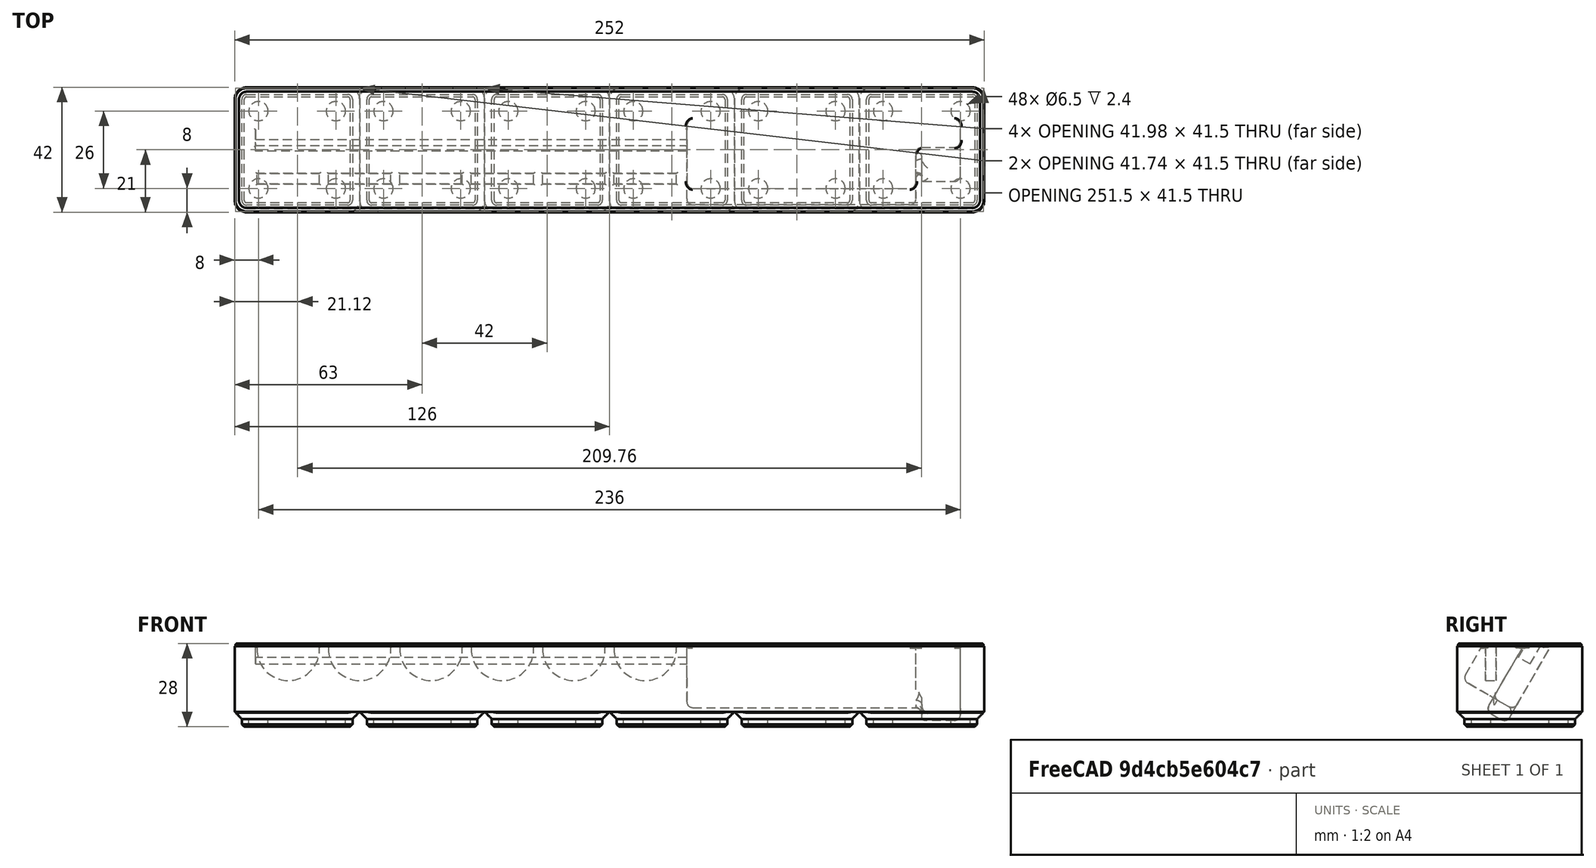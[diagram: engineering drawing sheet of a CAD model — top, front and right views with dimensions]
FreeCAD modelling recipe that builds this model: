
FCSTD DOCUMENT  (FreeCAD 0.21R)
Label: MyGridfinity 6x1x4
License: Creative Commons Attribution
LicenseURL: http://creativecommons.org/licenses/by/4.0/
objects: Sketcher::SketchObject×15, PartDesign::Pocket×5, PartDesign::LinearPattern×3, PartDesign::Plane×2, PartDesign::Pad×2, PartDesign::Body×2, PartDesign::FeatureBase×2, PartDesign::Fillet×2, App::FeaturePython×1, PartDesign::AdditivePipe×1, PartDesign::SubtractiveLoft×1, PartDesign::Hole×1, PartDesign::MultiTransform×1, Mesh::Feature×1, PartDesign::SubShapeBinder×1
note: 50 computed .brp shape members not serialized (recipe doc carries the construction recipe); baked Part::Feature solids carry a one-line shape summary decoded from their .brp

FEATURE [App::FeaturePython] dd  # WARN: FeaturePython — macro-defined, semantics opaque (R4)
  DynamicData = Created with DynamicData (v2.46) workbench. | This is a simple container object built | for holding custom properties.
  ddBase_screw_diameter = 3
  ddBase_screw_hole_depth = 2.6
  ddBottom_chamfer = 0.8
  ddCell_center = 21
  ddClearance = 0.25
  ddColumns = 6
  ddCorner_fillet = 4
  ddFrame_height = 5
  ddFrame_width = 2.4
  ddGrid_size = 42
  ddHeight = 4
  ddMagnet_diameter = 6.5
  ddMagnet_inset = 8
  ddMagnet_thickness = 2.4
  ddRows = 1
  ddSet_screw_holes = true
  ddStorage_height = 28
  ddStorage_height_unit = 7
  ddTotal_length = 42
  ddTotal_width = 252
  ddWall_thickness = 1.2
  expr: ddBase_screw_hole_depth = max(ddSet_screw_holes * (ddFrame_height - ddMagnet_thickness); 1e-06mm)
  expr: ddCell_center = ddGrid_size / 2
  expr: ddStorage_height = max(ddStorage_height_unit * ddHeight; ddFrame_height + ddWall_thickness)
  expr: ddStorage_height_unit = ddGrid_size / 6
  expr: ddTotal_length = ddRows * ddGrid_size
  expr: ddTotal_width = ddColumns * ddGrid_size
FEATURE [Sketcher::SketchObject] Sketch005  label="Sketch_storage_wall_profile"
  AttachmentOffset = pos=(0,0,21) rot=(0,0,1;0rad)
  FullyConstrained = true
  MapMode = 5
  Placement = pos=(21,-4.7e-15,4.7e-15) rot=(0.57735,0.57735,0.57735;2.0944rad)
  Support = -> [YZ_Plane001]
  expr: .AttachmentOffset.Base.z = dd.ddCell_center
  expr: Constraints[16] = dd.ddFrame_height - dd.ddClearance
  expr: Constraints[17] = dd.ddBottom_chamfer
  expr: Constraints[26] = dd.ddWall_thickness
  expr: Constraints[27] = dd.ddWall_thickness
  expr: Constraints[28] = dd.ddStorage_height
  expr: Constraints[47] = dd.ddWall_thickness
  expr: Constraints[6] = dd.ddClearance
  expr: Constraints[7] = dd.ddFrame_width - dd.ddClearance
  sketch-geometry (17):
    g0: LineSegment StartX=0.25 StartY=0 StartZ=0 EndX=0.25 EndY=27.4 EndZ=0
    g1: LineSegment StartX=0.25 StartY=27.4 StartZ=0 EndX=0.85 EndY=27.4 EndZ=0
    g2: LineSegment StartX=0.85 StartY=27.4 StartZ=0 EndX=0.425736 EndY=26.9757 EndZ=0
    g3: LineSegment StartX=0.425736 StartY=26.9757 StartZ=0 EndX=2.15 EndY=25.2515 EndZ=0
    g4: LineSegment StartX=2.15 StartY=25.2515 StartZ=0 EndX=0 EndY=27.4015 EndZ=0
    g5: LineSegment StartX=2.15 StartY=25.2515 StartZ=0 EndX=2.15 EndY=23.4515 EndZ=0
    g6: LineSegment StartX=2.15 StartY=23.4515 StartZ=0 EndX=2.95 EndY=22.6515 EndZ=0
    g7: LineSegment StartX=2.95 StartY=22.6515 StartZ=0 EndX=2.95 EndY=21.4515 EndZ=0
    g8: LineSegment StartX=2.95 StartY=21.4515 StartZ=0 EndX=1.45 EndY=19.9515 EndZ=0
    g9: LineSegment StartX=1.45 StartY=19.9515 StartZ=0 EndX=1.45 EndY=-8.04853 EndZ=0
    g10: LineSegment StartX=1.45 StartY=-8.04853 StartZ=0 EndX=0.25 EndY=-8.04853 EndZ=0
    g11: LineSegment StartX=0.85 StartY=27.4 StartZ=0 EndX=0.85 EndY=28 EndZ=0
    g12: LineSegment StartX=1.45 StartY=19.9515 StartZ=0 EndX=1.45 EndY=28 EndZ=0
    g13: LineSegment StartX=0.85 StartY=28 StartZ=0 EndX=1.45 EndY=28 EndZ=0
    g14: LineSegment StartX=0.25 StartY=-8.04853 StartZ=0 EndX=0.25 EndY=0 EndZ=0
    g15: ArcOfCircle CenterX=0.85 CenterY=27.4 CenterZ=0 NormalX=0 NormalY=0 NormalZ=1 AngleXU=0 Radius=0.6 StartAngle=1.5708 EndAngle=3.14159
    g16: ArcOfCircle CenterX=0.85 CenterY=27.4 CenterZ=0 NormalX=0 NormalY=0 NormalZ=1 AngleXU=0 Radius=0.6 StartAngle=3.92699 EndAngle=7.85398
  constraints (48):
    c: Vertical(g0)
    c: Coincident(g1,g0)
    c: Horizontal(g1)
    c: Coincident(g2,g1)
    c: Coincident(g3,g2)
    c: Perpendicular(g3,g2)
    c: DistanceX(g-1,g0) = 0.25
    c: DistanceX(g-1,g3) = 2.15
    c: Coincident(g4,g3)
    c: PointOnObject(g4,g-2)
    c: PointOnObject(g2,g4)
    c: Angle(g-2,g4) = 0.785398
    c: Coincident(g5,g3)
    c: Vertical(g5)
    c: Coincident(g6,g5)
    c: Parallel(g4,g6)
    c: DistanceY(g6,g4) = 4.75
    c: DistanceX(g5,g6) = 0.8
    c: Coincident(g7,g6)
    c: Vertical(g7)
    c: Coincident(g8,g7)
    c: Coincident(g9,g8)
    c: Vertical(g9)
    c: Coincident(g10,g9)
    c: Horizontal(g10)
    c: Perpendicular(g8,g4)
    c: DistanceY(g7,g6) = 1.2
    c: DistanceX(g0,g9) = 1.2
    c: DistanceY(g-1,g11) = 28
    c: Coincident(g12,g8)
    c: Vertical(g12)
    c: Coincident(g13,g11)
    c: Coincident(g13,g12)
    c: Horizontal(g13)
    c: PointOnObject(g0,g-1)
    c: Coincident(g14,g10)
    c: Coincident(g14,g0)
    c: Vertical(g14)
    c: Equal(g12,g14)
    c: Vertical(g11)
    c: Coincident(g15,g1)
    c: Coincident(g15,g0)
    c: Coincident(g15,g11)
    c: Coincident(g16,g15)
    c: Coincident(g16,g15)
    c: Coincident(g16,g3)
    c: Coincident(g11,g15)
    c: Diameter(g15) = 1.2
FEATURE [Sketcher::SketchObject] Sketch006  label="Sketch_storage_wall_path"
  FullyConstrained = true
  MapMode = 5
  Support = -> [XY_Plane001]
  expr: Constraints[21] = dd.ddCorner_fillet
  expr: Constraints[22] = dd.ddTotal_width
  expr: Constraints[23] = dd.ddTotal_length
  sketch-geometry (10):
    g0: ArcOfCircle CenterX=4 CenterY=4 CenterZ=0 NormalX=0 NormalY=0 NormalZ=1 AngleXU=0 Radius=4 StartAngle=3.14159 EndAngle=4.71239
    g1: LineSegment StartX=0 StartY=4 StartZ=0 EndX=0 EndY=38 EndZ=0
    g2: ArcOfCircle CenterX=4 CenterY=38 CenterZ=0 NormalX=0 NormalY=0 NormalZ=1 AngleXU=0 Radius=4 StartAngle=1.5708 EndAngle=3.14159
    g3: LineSegment StartX=4 StartY=42 StartZ=0 EndX=248 EndY=42 EndZ=0
    g4: ArcOfCircle CenterX=248 CenterY=38 CenterZ=0 NormalX=0 NormalY=0 NormalZ=1 AngleXU=0 Radius=4 StartAngle=0 EndAngle=1.5708
    g5: LineSegment StartX=252 StartY=38 StartZ=0 EndX=252 EndY=4 EndZ=0
    g6: ArcOfCircle CenterX=248 CenterY=4 CenterZ=0 NormalX=0 NormalY=0 NormalZ=1 AngleXU=0 Radius=4 StartAngle=4.71239 EndAngle=6.28319
    g7: LineSegment StartX=248 StartY=0 StartZ=0 EndX=4 EndY=0 EndZ=0
    g8: GeomPoint X=0 Y=0 Z=0
    g9: GeomPoint X=252 Y=42 Z=0
  constraints (24):
    c: Tangent(g0,g1) = 1.5708
    c: Tangent(g1,g2) = 1.5708
    c: Tangent(g2,g3) = 1.5708
    c: Tangent(g3,g4) = 1.5708
    c: Tangent(g4,g5) = 1.5708
    c: Tangent(g5,g6) = 1.5708
    c: Tangent(g6,g7) = 1.5708
    c: Tangent(g7,g0) = 1.5708
    c: Horizontal(g3)
    c: Horizontal(g7)
    c: Vertical(g1)
    c: Vertical(g5)
    c: Equal(g0,g2)
    c: Equal(g2,g4)
    c: Equal(g4,g6)
    c: PointOnObject(g8,g1)
    c: PointOnObject(g8,g7)
    c: PointOnObject(g9,g3)
    c: PointOnObject(g9,g5)
    c: PointOnObject(g8,g-2)
    c: PointOnObject(g0,g-1)
    c: Radius(g0) = 4
    c: DistanceX(g0,g5) = 252
    c: DistanceY(g0,g2) = 42
FEATURE [PartDesign::AdditivePipe] AdditivePipe  label="AdditivePipe_storage_wall"
  AuxilleryCurvelinear = true
  AuxillerySpineTangent = false
  Binormal = (0,0,0)
  Mode = 0
  Placement = pos=(0,0,0) rot=(0.57735,0.57735,0.57735;2.0944rad)
  Profile = -> Sketch005
  Refine = true
  Spine = -> Sketch006
  SpineTangent = false
  Transformation = 0
  Transition = 0
FEATURE [PartDesign::Plane] DatumPlane  label="DatumPlane_frame_height"
  AttachmentOffset = pos=(0,0,5) rot=(0,0,1;0rad)
  Length = 304.246
  MapMode = 5
  Placement = pos=(0,0,5) rot=(0,0,1;0rad)
  ResizeMode = 0
  Support = -> [XY_Plane001]
  Width = 94.2463
  expr: .AttachmentOffset.Base.z = dd.ddFrame_height
FEATURE [Sketcher::SketchObject] Sketch007  label="Sketch_trim_wall_bottom"
  FullyConstrained = true
  MapMode = 5
  Placement = pos=(0,0,5) rot=(0,0,1;0rad)
  Support = -> [DatumPlane]
  expr: Constraints[7] = dd.ddTotal_width + 10mm
  expr: Constraints[8] = dd.ddTotal_length + 10mm
  sketch-geometry (4):
    g0: LineSegment StartX=-5 StartY=-5 StartZ=0 EndX=257 EndY=-5 EndZ=0
    g1: LineSegment StartX=257 StartY=-5 StartZ=0 EndX=257 EndY=47 EndZ=0
    g2: LineSegment StartX=257 StartY=47 StartZ=0 EndX=-5 EndY=47 EndZ=0
    g3: LineSegment StartX=-5 StartY=47 StartZ=0 EndX=-5 EndY=-5 EndZ=0
  constraints (12):
    c: Coincident(g0,g1)
    c: Coincident(g1,g2)
    c: Coincident(g2,g3)
    c: Horizontal(g0)
    c: Horizontal(g2)
    c: Vertical(g1)
    c: Vertical(g3)
    c: DistanceX(g0,g0) = 262
    c: DistanceY(g0,g2) = 52
    c: Coincident(g3,g0)
    c: DistanceX(g0,g-1) = 5
    c: DistanceY(g0,g-1) = 5
FEATURE [PartDesign::Pocket] Pocket  label="Pocket_trim_wall_bottom"
  BaseFeature = -> AdditivePipe
  Direction = (0,0,-1)
  Length = 5
  Length2 = 5
  Placement = pos=(0,0,0) rot=(0.57735,0.57735,0.57735;2.0944rad)
  Profile = -> Sketch007
  ReferenceAxis = -> Sketch007 [N_Axis]
  Refine = true
  Type = 1
FEATURE [Sketcher::SketchObject] Sketch008  label="Sketch_storage_stock"
  FullyConstrained = true
  MapMode = 5
  Support = -> [XY_Plane001]
  expr: Constraints[19] = dd.ddClearance
  expr: Constraints[20] = dd.ddClearance
  expr: Constraints[21] = dd.ddCorner_fillet
  expr: Constraints[22] = dd.ddTotal_width - 2 * dd.ddCorner_fillet
  expr: Constraints[23] = dd.ddTotal_length - 2 * dd.ddCorner_fillet
  sketch-geometry (10):
    g0: ArcOfCircle CenterX=4 CenterY=4 CenterZ=0 NormalX=0 NormalY=0 NormalZ=1 AngleXU=0 Radius=3.75 StartAngle=3.14159 EndAngle=4.71239
    g1: LineSegment StartX=0.25 StartY=4 StartZ=0 EndX=0.25 EndY=38 EndZ=0
    g2: ArcOfCircle CenterX=4 CenterY=38 CenterZ=0 NormalX=0 NormalY=0 NormalZ=1 AngleXU=0 Radius=3.75 StartAngle=1.5708 EndAngle=3.14159
    g3: LineSegment StartX=4 StartY=41.75 StartZ=0 EndX=248 EndY=41.75 EndZ=0
    g4: ArcOfCircle CenterX=248 CenterY=38 CenterZ=0 NormalX=0 NormalY=0 NormalZ=1 AngleXU=0 Radius=3.75 StartAngle=0 EndAngle=1.5708
    g5: LineSegment StartX=251.75 StartY=38 StartZ=0 EndX=251.75 EndY=4 EndZ=0
    g6: ArcOfCircle CenterX=248 CenterY=4 CenterZ=0 NormalX=0 NormalY=0 NormalZ=1 AngleXU=0 Radius=3.75 StartAngle=4.71239 EndAngle=6.28319
    g7: LineSegment StartX=248 StartY=0.25 StartZ=0 EndX=4 EndY=0.25 EndZ=0
    g8: GeomPoint X=0.25 Y=0.25 Z=0
    g9: GeomPoint X=251.75 Y=41.75 Z=0
  constraints (24):
    c: Tangent(g0,g1) = 1.5708
    c: Tangent(g1,g2) = 1.5708
    c: Tangent(g2,g3) = 1.5708
    c: Tangent(g3,g4) = 1.5708
    c: Tangent(g4,g5) = 1.5708
    c: Tangent(g5,g6) = 1.5708
    c: Tangent(g6,g7) = 1.5708
    c: Tangent(g7,g0) = 1.5708
    c: Horizontal(g3)
    c: Horizontal(g7)
    c: Vertical(g1)
    c: Vertical(g5)
    c: Equal(g0,g2)
    c: Equal(g2,g4)
    c: Equal(g4,g6)
    c: PointOnObject(g8,g1)
    c: PointOnObject(g8,g7)
    c: PointOnObject(g9,g3)
    c: PointOnObject(g9,g5)
    c: DistanceX(g-1,g0) = 0.25
    c: DistanceY(g-1,g0) = 0.25
    c: DistanceX(g-1,g0) = 4
    c: DistanceX(g2,g4) = 244
    c: DistanceY(g6,g4) = 34
FEATURE [PartDesign::Pad] Pad001  label="Pad_storage_stock"
  BaseFeature = -> Pocket
  Direction = (0,0,1)
  Length = 6.2
  Length2 = 10
  Placement = pos=(0,0,0) rot=(0.57735,0.57735,0.57735;2.0944rad)
  Profile = -> Sketch008
  ReferenceAxis = -> Sketch008 [N_Axis]
  Refine = true
  Type = 0
  expr: Length = dd.ddFrame_height + dd.ddWall_thickness
FEATURE [Sketcher::SketchObject] Sketch009  label="Sketch_storage_cell_cutout_top"
  AttachmentOffset = pos=(0,0,5) rot=(0,0,1;0rad)
  FullyConstrained = true
  MapMode = 5
  Placement = pos=(0,0,5) rot=(0,0,1;0rad)
  Support = -> [XY_Plane001]
  expr: .AttachmentOffset.Base.z = dd.ddFrame_height
  expr: Constraints[19] = dd.ddCorner_fillet - 1e-06mm
  expr: Constraints[20] = dd.ddCorner_fillet
  expr: Constraints[21] = dd.ddCorner_fillet
  expr: Constraints[31] = dd.ddCorner_fillet
  expr: Constraints[32] = dd.ddCorner_fillet
  expr: Constraints[33] = dd.ddGrid_size
  expr: Constraints[34] = dd.ddGrid_size
  sketch-geometry (14):
    g0: ArcOfCircle CenterX=4 CenterY=4 CenterZ=0 NormalX=0 NormalY=0 NormalZ=1 AngleXU=0 Radius=4 StartAngle=3.14159 EndAngle=4.71239
    g1: LineSegment StartX=1e-06 StartY=4 StartZ=0 EndX=1e-06 EndY=38 EndZ=0
    g2: ArcOfCircle CenterX=4 CenterY=38 CenterZ=0 NormalX=0 NormalY=0 NormalZ=1 AngleXU=0 Radius=4 StartAngle=1.5708 EndAngle=3.14159
    g3: LineSegment StartX=4 StartY=42 StartZ=0 EndX=38 EndY=42 EndZ=0
    g4: ArcOfCircle CenterX=38 CenterY=38 CenterZ=0 NormalX=0 NormalY=0 NormalZ=1 AngleXU=0 Radius=4 StartAngle=-9e-16 EndAngle=1.5708
    g5: LineSegment StartX=42 StartY=38 StartZ=0 EndX=42 EndY=4 EndZ=0
    g6: ArcOfCircle CenterX=38 CenterY=4 CenterZ=0 NormalX=0 NormalY=0 NormalZ=1 AngleXU=0 Radius=4 StartAngle=4.71239 EndAngle=6.28319
    g7: LineSegment StartX=38 StartY=1e-06 StartZ=0 EndX=4 EndY=1e-06 EndZ=0
    g8: GeomPoint X=1e-06 Y=1e-06 Z=0
    g9: GeomPoint X=42 Y=42 Z=0
    g10: LineSegment StartX=0 StartY=0 StartZ=0 EndX=42 EndY=0 EndZ=0
    g11: LineSegment StartX=42 StartY=0 StartZ=0 EndX=42 EndY=42 EndZ=0
    g12: LineSegment StartX=42 StartY=42 StartZ=0 EndX=0 EndY=42 EndZ=0
    g13: LineSegment StartX=0 StartY=42 StartZ=0 EndX=0 EndY=0 EndZ=0
  constraints (35):
    c: Tangent(g0,g1) = 1.5708
    c: Tangent(g1,g2) = 1.5708
    c: Tangent(g2,g3) = 1.5708
    c: Tangent(g3,g4) = 1.5708
    c: Tangent(g4,g5) = 1.5708
    c: Tangent(g5,g6) = 1.5708
    c: Tangent(g6,g7) = 1.5708
    c: Tangent(g7,g0) = 1.5708
    c: Horizontal(g3)
    c: Horizontal(g7)
    c: Vertical(g1)
    c: Vertical(g5)
    c: Equal(g0,g2)
    c: Equal(g2,g4)
    c: Equal(g4,g6)
    c: PointOnObject(g8,g1)
    c: PointOnObject(g8,g7)
    c: PointOnObject(g9,g3)
    c: PointOnObject(g9,g5)
    c: Radius(g0) = 4
    c: DistanceX(g-1,g0) = 4
    c: DistanceY(g-1,g0) = 4
    c: Coincident(g10,g11)
    c: Coincident(g11,g12)
    c: Coincident(g12,g13)
    c: Coincident(g13,g10)
    c: Horizontal(g10)
    c: Horizontal(g12)
    c: Vertical(g11)
    c: Vertical(g13)
    c: Coincident(g10,g-1)
    c: DistanceX(g6,g10) = 4
    c: DistanceY(g2,g12) = 4
    c: DistanceX(g10,g10) = 42
    c: DistanceY(g10,g12) = 42
FEATURE [Sketcher::SketchObject] Sketch010  label="Sketch_storage_cell_cutout_top_chamfer"
  AttachmentOffset = pos=(0,0,2.6) rot=(0,0,1;0rad)
  FullyConstrained = true
  MapMode = 5
  Placement = pos=(0,0,2.6) rot=(0,0,1;0rad)
  Support = -> [XY_Plane001]
  expr: .AttachmentOffset.Base.z = dd.ddFrame_height - dd.ddFrame_width
  expr: Constraints[19] = Sketch009.Constraints[19] - dd.ddFrame_width
  expr: Constraints[20] = Sketch009.Constraints[20]
  expr: Constraints[21] = Sketch009.Constraints[21]
  expr: Constraints[31] = Sketch009.Constraints[31]
  expr: Constraints[32] = Sketch009.Constraints[32]
  expr: Constraints[33] = Sketch009.Constraints[33]
  expr: Constraints[34] = Sketch009.Constraints[34]
  sketch-geometry (14):
    g0: ArcOfCircle CenterX=4 CenterY=4 CenterZ=0 NormalX=0 NormalY=0 NormalZ=1 AngleXU=0 Radius=1.6 StartAngle=3.14159 EndAngle=4.71239
    g1: LineSegment StartX=2.4 StartY=4 StartZ=0 EndX=2.4 EndY=38 EndZ=0
    g2: ArcOfCircle CenterX=4 CenterY=38 CenterZ=0 NormalX=0 NormalY=0 NormalZ=1 AngleXU=0 Radius=1.6 StartAngle=1.5708 EndAngle=3.14159
    g3: LineSegment StartX=4 StartY=39.6 StartZ=0 EndX=38 EndY=39.6 EndZ=0
    g4: ArcOfCircle CenterX=38 CenterY=38 CenterZ=0 NormalX=0 NormalY=0 NormalZ=1 AngleXU=0 Radius=1.6 StartAngle=3.81e-14 EndAngle=1.5708
    g5: LineSegment StartX=39.6 StartY=38 StartZ=0 EndX=39.6 EndY=4 EndZ=0
    g6: ArcOfCircle CenterX=38 CenterY=4 CenterZ=0 NormalX=0 NormalY=0 NormalZ=1 AngleXU=0 Radius=1.6 StartAngle=4.71239 EndAngle=6.28319
    g7: LineSegment StartX=38 StartY=2.4 StartZ=0 EndX=4 EndY=2.4 EndZ=0
    g8: GeomPoint X=2.4 Y=2.4 Z=0
    g9: GeomPoint X=39.6 Y=39.6 Z=0
    g10: LineSegment StartX=0 StartY=0 StartZ=0 EndX=42 EndY=0 EndZ=0
    g11: LineSegment StartX=42 StartY=0 StartZ=0 EndX=42 EndY=42 EndZ=0
    g12: LineSegment StartX=42 StartY=42 StartZ=0 EndX=0 EndY=42 EndZ=0
    g13: LineSegment StartX=0 StartY=42 StartZ=0 EndX=0 EndY=0 EndZ=0
  constraints (35):
    c: Tangent(g0,g1) = 1.5708
    c: Tangent(g1,g2) = 1.5708
    c: Tangent(g2,g3) = 1.5708
    c: Tangent(g3,g4) = 1.5708
    c: Tangent(g4,g5) = 1.5708
    c: Tangent(g5,g6) = 1.5708
    c: Tangent(g6,g7) = 1.5708
    c: Tangent(g7,g0) = 1.5708
    c: Horizontal(g3)
    c: Horizontal(g7)
    c: Vertical(g1)
    c: Vertical(g5)
    c: Equal(g0,g2)
    c: Equal(g2,g4)
    c: Equal(g4,g6)
    c: PointOnObject(g8,g1)
    c: PointOnObject(g8,g7)
    c: PointOnObject(g9,g3)
    c: PointOnObject(g9,g5)
    c: Radius(g0) = 1.6
    c: DistanceX(g-1,g0) = 4
    c: DistanceY(g-1,g0) = 4
    c: Coincident(g10,g11)
    c: Coincident(g11,g12)
    c: Coincident(g12,g13)
    c: Coincident(g13,g10)
    c: Horizontal(g10)
    c: Horizontal(g12)
    c: Vertical(g11)
    c: Vertical(g13)
    c: Coincident(g10,g-1)
    c: DistanceX(g6,g10) = 4
    c: DistanceY(g2,g12) = 4
    c: DistanceX(g10,g10) = 42
    c: DistanceY(g10,g12) = 42
FEATURE [Sketcher::SketchObject] Sketch011  label="Sketch_storage_cell_cutout_bottom_chamfer"
  AttachmentOffset = pos=(0,0,0.8) rot=(0,0,1;0rad)
  FullyConstrained = true
  MapMode = 5
  Placement = pos=(0,0,0.8) rot=(0,0,1;0rad)
  Support = -> [XY_Plane001]
  expr: .AttachmentOffset.Base.z = dd.ddBottom_chamfer
  expr: Constraints[19] = Sketch010.Constraints[19]
  expr: Constraints[20] = Sketch010.Constraints[20]
  expr: Constraints[21] = Sketch010.Constraints[21]
  expr: Constraints[31] = Sketch010.Constraints[31]
  expr: Constraints[32] = Sketch010.Constraints[32]
  expr: Constraints[33] = Sketch010.Constraints[33]
  expr: Constraints[34] = Sketch010.Constraints[34]
  sketch-geometry (14):
    g0: ArcOfCircle CenterX=4 CenterY=4 CenterZ=0 NormalX=0 NormalY=0 NormalZ=1 AngleXU=0 Radius=1.6 StartAngle=3.14159 EndAngle=4.71239
    g1: LineSegment StartX=2.4 StartY=4 StartZ=0 EndX=2.4 EndY=38 EndZ=0
    g2: ArcOfCircle CenterX=4 CenterY=38 CenterZ=0 NormalX=0 NormalY=0 NormalZ=1 AngleXU=0 Radius=1.6 StartAngle=1.5708 EndAngle=3.14159
    g3: LineSegment StartX=4 StartY=39.6 StartZ=0 EndX=38 EndY=39.6 EndZ=0
    g4: ArcOfCircle CenterX=38 CenterY=38 CenterZ=0 NormalX=0 NormalY=0 NormalZ=1 AngleXU=0 Radius=1.6 StartAngle=3.81e-14 EndAngle=1.5708
    g5: LineSegment StartX=39.6 StartY=38 StartZ=0 EndX=39.6 EndY=4 EndZ=0
    g6: ArcOfCircle CenterX=38 CenterY=4 CenterZ=0 NormalX=0 NormalY=0 NormalZ=1 AngleXU=0 Radius=1.6 StartAngle=4.71239 EndAngle=6.28319
    g7: LineSegment StartX=38 StartY=2.4 StartZ=0 EndX=4 EndY=2.4 EndZ=0
    g8: GeomPoint X=2.4 Y=2.4 Z=0
    g9: GeomPoint X=39.6 Y=39.6 Z=0
    g10: LineSegment StartX=0 StartY=0 StartZ=0 EndX=42 EndY=0 EndZ=0
    g11: LineSegment StartX=42 StartY=0 StartZ=0 EndX=42 EndY=42 EndZ=0
    g12: LineSegment StartX=42 StartY=42 StartZ=0 EndX=0 EndY=42 EndZ=0
    g13: LineSegment StartX=0 StartY=42 StartZ=0 EndX=0 EndY=0 EndZ=0
  constraints (35):
    c: Tangent(g0,g1) = 1.5708
    c: Tangent(g1,g2) = 1.5708
    c: Tangent(g2,g3) = 1.5708
    c: Tangent(g3,g4) = 1.5708
    c: Tangent(g4,g5) = 1.5708
    c: Tangent(g5,g6) = 1.5708
    c: Tangent(g6,g7) = 1.5708
    c: Tangent(g7,g0) = 1.5708
    c: Horizontal(g3)
    c: Horizontal(g7)
    c: Vertical(g1)
    c: Vertical(g5)
    c: Equal(g0,g2)
    c: Equal(g2,g4)
    c: Equal(g4,g6)
    c: PointOnObject(g8,g1)
    c: PointOnObject(g8,g7)
    c: PointOnObject(g9,g3)
    c: PointOnObject(g9,g5)
    c: Radius(g0) = 1.6
    c: DistanceX(g-1,g0) = 4
    c: DistanceY(g-1,g0) = 4
    c: Coincident(g10,g11)
    c: Coincident(g11,g12)
    c: Coincident(g12,g13)
    c: Coincident(g13,g10)
    c: Horizontal(g10)
    c: Horizontal(g12)
    c: Vertical(g11)
    c: Vertical(g13)
    c: Coincident(g10,g-1)
    c: DistanceX(g6,g10) = 4
    c: DistanceY(g2,g12) = 4
    c: DistanceX(g10,g10) = 42
    c: DistanceY(g10,g12) = 42
FEATURE [Sketcher::SketchObject] Sketch012  label="Sketch_storage_cell_cutout_bottom"
  FullyConstrained = true
  MapMode = 5
  Support = -> [XY_Plane001]
  expr: Constraints[19] = Sketch011.Constraints[19] - dd.ddBottom_chamfer
  expr: Constraints[20] = Sketch011.Constraints[20]
  expr: Constraints[21] = Sketch011.Constraints[21]
  expr: Constraints[31] = Sketch011.Constraints[31]
  expr: Constraints[32] = Sketch011.Constraints[32]
  expr: Constraints[33] = Sketch011.Constraints[33]
  expr: Constraints[34] = Sketch011.Constraints[34]
  sketch-geometry (14):
    g0: ArcOfCircle CenterX=4 CenterY=4 CenterZ=0 NormalX=0 NormalY=0 NormalZ=1 AngleXU=0 Radius=0.799999 StartAngle=3.14159 EndAngle=4.71239
    g1: LineSegment StartX=3.2 StartY=4 StartZ=0 EndX=3.2 EndY=38 EndZ=0
    g2: ArcOfCircle CenterX=4 CenterY=38 CenterZ=0 NormalX=0 NormalY=0 NormalZ=1 AngleXU=0 Radius=0.799999 StartAngle=1.5708 EndAngle=3.14159
    g3: LineSegment StartX=4 StartY=38.8 StartZ=0 EndX=38 EndY=38.8 EndZ=0
    g4: ArcOfCircle CenterX=38 CenterY=38 CenterZ=0 NormalX=0 NormalY=0 NormalZ=1 AngleXU=0 Radius=0.799999 StartAngle=-2.7e-15 EndAngle=1.5708
    g5: LineSegment StartX=38.8 StartY=38 StartZ=0 EndX=38.8 EndY=4 EndZ=0
    g6: ArcOfCircle CenterX=38 CenterY=4 CenterZ=0 NormalX=0 NormalY=0 NormalZ=1 AngleXU=0 Radius=0.799999 StartAngle=4.71239 EndAngle=6.28319
    g7: LineSegment StartX=38 StartY=3.2 StartZ=0 EndX=4 EndY=3.2 EndZ=0
    g8: GeomPoint X=3.2 Y=3.2 Z=0
    g9: GeomPoint X=38.8 Y=38.8 Z=0
    g10: LineSegment StartX=0 StartY=0 StartZ=0 EndX=42 EndY=0 EndZ=0
    g11: LineSegment StartX=42 StartY=0 StartZ=0 EndX=42 EndY=42 EndZ=0
    g12: LineSegment StartX=42 StartY=42 StartZ=0 EndX=0 EndY=42 EndZ=0
    g13: LineSegment StartX=0 StartY=42 StartZ=0 EndX=0 EndY=0 EndZ=0
  constraints (35):
    c: Tangent(g0,g1) = 1.5708
    c: Tangent(g1,g2) = 1.5708
    c: Tangent(g2,g3) = 1.5708
    c: Tangent(g3,g4) = 1.5708
    c: Tangent(g4,g5) = 1.5708
    c: Tangent(g5,g6) = 1.5708
    c: Tangent(g6,g7) = 1.5708
    c: Tangent(g7,g0) = 1.5708
    c: Horizontal(g3)
    c: Horizontal(g7)
    c: Vertical(g1)
    c: Vertical(g5)
    c: Equal(g0,g2)
    c: Equal(g2,g4)
    c: Equal(g4,g6)
    c: PointOnObject(g8,g1)
    c: PointOnObject(g8,g7)
    c: PointOnObject(g9,g3)
    c: PointOnObject(g9,g5)
    c: Radius(g0) = 0.799999
    c: DistanceX(g-1,g0) = 4
    c: DistanceY(g-1,g0) = 4
    c: Coincident(g10,g11)
    c: Coincident(g11,g12)
    c: Coincident(g12,g13)
    c: Coincident(g13,g10)
    c: Horizontal(g10)
    c: Horizontal(g12)
    c: Vertical(g11)
    c: Vertical(g13)
    c: Coincident(g10,g-1)
    c: DistanceX(g6,g10) = 4
    c: DistanceY(g2,g12) = 4
    c: DistanceX(g10,g10) = 42
    c: DistanceY(g10,g12) = 42
FEATURE [PartDesign::SubtractiveLoft] SubtractiveLoft001  label="SubtractiveLoft_storage_cell_cutout"
  BaseFeature = -> Pad001
  Closed = false
  Placement = pos=(0,0,0) rot=(0.57735,0.57735,0.57735;2.0944rad)
  Profile = -> Sketch009
  Refine = true
  Ruled = true
  Sections = -> [Sketch010,Sketch011,Sketch012]
FEATURE [Sketcher::SketchObject] Sketch013  label="Sketch_base_magnets"
  FullyConstrained = true
  MapMode = 5
  Support = -> [XY_Plane001]
  expr: Constraints[21] = dd.ddMagnet_inset
  expr: Constraints[22] = dd.ddGrid_size
  expr: Constraints[23] = dd.ddGrid_size
  expr: Constraints[31] = dd.ddMagnet_diameter
  sketch-geometry (14):
    g0: ArcOfCircle CenterX=8 CenterY=8 CenterZ=0 NormalX=0 NormalY=0 NormalZ=1 AngleXU=0 Radius=8 StartAngle=3.14159 EndAngle=4.71239
    g1: LineSegment StartX=0 StartY=8 StartZ=0 EndX=0 EndY=34 EndZ=0
    g2: ArcOfCircle CenterX=8 CenterY=34 CenterZ=0 NormalX=0 NormalY=0 NormalZ=1 AngleXU=0 Radius=8 StartAngle=1.5708 EndAngle=3.14159
    g3: LineSegment StartX=8 StartY=42 StartZ=0 EndX=34 EndY=42 EndZ=0
    g4: ArcOfCircle CenterX=34 CenterY=34 CenterZ=0 NormalX=0 NormalY=0 NormalZ=1 AngleXU=0 Radius=8 StartAngle=0 EndAngle=1.5708
    g5: LineSegment StartX=42 StartY=34 StartZ=0 EndX=42 EndY=8 EndZ=0
    g6: ArcOfCircle CenterX=34 CenterY=8 CenterZ=0 NormalX=0 NormalY=0 NormalZ=1 AngleXU=0 Radius=8 StartAngle=4.71239 EndAngle=6.28319
    g7: LineSegment StartX=34 StartY=-1.8e-15 StartZ=0 EndX=8 EndY=-1.8e-15 EndZ=0
    g8: GeomPoint X=0 Y=0 Z=0
    g9: GeomPoint X=42 Y=42 Z=0
    g10: Circle CenterX=8 CenterY=34 CenterZ=0 NormalX=0 NormalY=0 NormalZ=1 AngleXU=0 Radius=3.25
    g11: Circle CenterX=34 CenterY=34 CenterZ=0 NormalX=0 NormalY=0 NormalZ=1 AngleXU=0 Radius=3.25
    g12: Circle CenterX=8 CenterY=8 CenterZ=0 NormalX=0 NormalY=0 NormalZ=1 AngleXU=0 Radius=3.25
    g13: Circle CenterX=34 CenterY=8 CenterZ=0 NormalX=0 NormalY=0 NormalZ=1 AngleXU=0 Radius=3.25
  constraints (32):
    c: Tangent(g0,g1) = 1.5708
    c: Tangent(g1,g2) = 1.5708
    c: Tangent(g2,g3) = 1.5708
    c: Tangent(g3,g4) = 1.5708
    c: Tangent(g4,g5) = 1.5708
    c: Tangent(g5,g6) = 1.5708
    c: Tangent(g6,g7) = 1.5708
    c: Tangent(g7,g0) = 1.5708
    c: Horizontal(g3)
    c: Horizontal(g7)
    c: Vertical(g1)
    c: Vertical(g5)
    c: Equal(g0,g2)
    c: Equal(g2,g4)
    c: Equal(g4,g6)
    c: PointOnObject(g8,g1)
    c: PointOnObject(g8,g7)
    c: PointOnObject(g9,g3)
    c: PointOnObject(g9,g5)
    c: PointOnObject(g0,g-2)
    c: PointOnObject(g0,g-1)
    c: DistanceX(g8,g0) = 8
    c: DistanceX(g0,g5) = 42
    c: DistanceY(g0,g2) = 42
    c: Coincident(g10,g2)
    c: Coincident(g11,g4)
    c: Coincident(g12,g0)
    c: Coincident(g13,g6)
    c: Equal(g12,g10)
    c: Equal(g12,g11)
    c: Equal(g12,g13)
    c: Diameter(g12) = 6.5
FEATURE [PartDesign::Hole] Hole  label="Hole_base_magnets"
  BaseFeature = -> SubtractiveLoft001
  CustomThreadClearance = 0
  Depth = 2.4
  DepthType = 0
  Diameter = 6.5
  DrillForDepth = false
  DrillPoint = 0
  DrillPointAngle = 118
  HoleCutCountersinkAngle = 90
  HoleCutCustomValues = false
  HoleCutDepth = 0
  HoleCutDiameter = 0
  HoleCutType = 0
  ModelThread = false
  Placement = pos=(0,0,0) rot=(0.57735,0.57735,0.57735;2.0944rad)
  Profile = -> Sketch013
  Refine = true
  Reversed = true
  Tapered = false
  TaperedAngle = 90
  ThreadClass = 0
  ThreadDepth = 2.4
  ThreadDepthType = 0
  ThreadDirection = 0
  ThreadFit = 0
  ThreadSize = 0
  ThreadType = 0
  Threaded = false
  UseCustomThreadClearance = false
  expr: Depth = dd.ddMagnet_thickness
  expr: Diameter = dd.ddMagnet_diameter
FEATURE [Sketcher::SketchObject] Sketch014  label="Sketch_base_screw_holes"
  AttachmentOffset = pos=(0,0,2.4) rot=(0,0,1;0rad)
  FullyConstrained = true
  MapMode = 5
  Placement = pos=(0,0,2.4) rot=(0,0,1;0rad)
  Support = -> [XY_Plane001]
  expr: .AttachmentOffset.Base.z = dd.ddMagnet_thickness
  expr: Constraints[21] = Sketch013.Constraints[21]
  expr: Constraints[22] = Sketch013.Constraints[22]
  expr: Constraints[23] = Sketch013.Constraints[23]
  expr: Constraints[31] = dd.ddBase_screw_diameter
  sketch-geometry (14):
    g0: ArcOfCircle CenterX=8 CenterY=8 CenterZ=0 NormalX=0 NormalY=0 NormalZ=1 AngleXU=0 Radius=8 StartAngle=3.14159 EndAngle=4.71239
    g1: LineSegment StartX=-1.8e-15 StartY=8 StartZ=0 EndX=-1.8e-15 EndY=34 EndZ=0
    g2: ArcOfCircle CenterX=8 CenterY=34 CenterZ=0 NormalX=0 NormalY=0 NormalZ=1 AngleXU=0 Radius=8 StartAngle=1.5708 EndAngle=3.14159
    g3: LineSegment StartX=8 StartY=42 StartZ=0 EndX=34 EndY=42 EndZ=0
    g4: ArcOfCircle CenterX=34 CenterY=34 CenterZ=0 NormalX=0 NormalY=0 NormalZ=1 AngleXU=0 Radius=8 StartAngle=0 EndAngle=1.5708
    g5: LineSegment StartX=42 StartY=34 StartZ=0 EndX=42 EndY=8 EndZ=0
    g6: ArcOfCircle CenterX=34 CenterY=8 CenterZ=0 NormalX=0 NormalY=0 NormalZ=1 AngleXU=0 Radius=8 StartAngle=4.71239 EndAngle=6.28319
    g7: LineSegment StartX=34 StartY=-1.8e-15 StartZ=0 EndX=8 EndY=-1.8e-15 EndZ=0
    g8: GeomPoint X=0 Y=0 Z=0
    g9: GeomPoint X=42 Y=42 Z=0
    g10: Circle CenterX=8 CenterY=34 CenterZ=0 NormalX=0 NormalY=0 NormalZ=1 AngleXU=0 Radius=1.5
    g11: Circle CenterX=34 CenterY=34 CenterZ=0 NormalX=0 NormalY=0 NormalZ=1 AngleXU=0 Radius=1.5
    g12: Circle CenterX=8 CenterY=8 CenterZ=0 NormalX=0 NormalY=0 NormalZ=1 AngleXU=0 Radius=1.5
    g13: Circle CenterX=34 CenterY=8 CenterZ=0 NormalX=0 NormalY=0 NormalZ=1 AngleXU=0 Radius=1.5
  constraints (32):
    c: Tangent(g0,g1) = 1.5708
    c: Tangent(g1,g2) = 1.5708
    c: Tangent(g2,g3) = 1.5708
    c: Tangent(g3,g4) = 1.5708
    c: Tangent(g4,g5) = 1.5708
    c: Tangent(g5,g6) = 1.5708
    c: Tangent(g6,g7) = 1.5708
    c: Tangent(g7,g0) = 1.5708
    c: Horizontal(g3)
    c: Horizontal(g7)
    c: Vertical(g1)
    c: Vertical(g5)
    c: Equal(g0,g2)
    c: Equal(g2,g4)
    c: Equal(g4,g6)
    c: PointOnObject(g8,g1)
    c: PointOnObject(g8,g7)
    c: PointOnObject(g9,g3)
    c: PointOnObject(g9,g5)
    c: PointOnObject(g0,g-2)
    c: PointOnObject(g0,g-1)
    c: DistanceX(g8,g0) = 8
    c: DistanceX(g0,g5) = 42
    c: DistanceY(g0,g2) = 42
    c: Coincident(g10,g2)
    c: Coincident(g11,g4)
    c: Coincident(g12,g0)
    c: Coincident(g13,g6)
    c: Equal(g12,g10)
    c: Equal(g12,g11)
    c: Equal(g12,g13)
    c: Diameter(g12) = 3
FEATURE [PartDesign::LinearPattern] LinearPattern002  label="LinearPattern_storage_grid_x"
  Direction = -> X_Axis001
  Length = 210
  Occurrences = 6
  Placement = pos=(0,0,0) rot=(0.57735,0.57735,0.57735;2.0944rad)
  Refine = true
  expr: Length = max(dd.ddTotal_width - dd.ddGrid_size; 1e-06mm)
  expr: Occurrences = max(dd.ddColumns; 2)
FEATURE [PartDesign::LinearPattern] LinearPattern003  label="LinearPattern_storage_grid_y"
  Direction = -> Y_Axis001
  Length = 42
  Occurrences = 1
  Placement = pos=(0,0,0) rot=(0.57735,0.57735,0.57735;2.0944rad)
  Refine = true
  expr: Length = max(dd.ddTotal_length - dd.ddGrid_size; dd.ddGrid_size)
  expr: Occurrences = dd.ddRows
FEATURE [PartDesign::MultiTransform] MultiTransform001  label="MultiTransform_storage_grid"
  BaseFeature = -> Hole
  Originals = -> [SubtractiveLoft001,Hole]
  Placement = pos=(0,0,0) rot=(0.57735,0.57735,0.57735;2.0944rad)
  Refine = true
  Transformations = -> [LinearPattern002,LinearPattern003]
FEATURE [Mesh::Feature] Gridfinity_Caliper_Holder  label="Gridfinity Caliper Holder"
  Placement = pos=(21,21,5) rot=(0,0,1;4.71239rad)
FEATURE [Sketcher::SketchObject] Sketch019
  AttachmentOffset = pos=(0,0,-13) rot=(0,0,1;0rad)
  FullyConstrained = true
  MapMode = 5
  Placement = pos=(0,13,2.9e-15) rot=(1,0,0;1.5708rad)
  Support = -> [XZ_Plane002]
  sketch-geometry (1):
    g0: Circle CenterX=18 CenterY=26 CenterZ=0 NormalX=0 NormalY=0 NormalZ=1 AngleXU=0 Radius=10.5
  constraints (3):
    c: Diameter(g0) = 21
    c: DistanceY(g-1,g0) = 26
    c: DistanceX(g-1,g0) = 18
FEATURE [PartDesign::SubShapeBinder] Binder
  BindCopyOnChange = 0
  BindMode = 0
  ClaimChildren = false
  Context = -> Body001 [Binder.]
  Fuse = false
  MakeFace = true
  OffsetFill = false
  OffsetIntersection = false
  OffsetJoinType = 0
  OffsetOpenResult = false
  PartialLoad = false
  Placement = pos=(0,0,4.99) rot=(0,0,1;0rad)
  Relative = false
  Support = -> [AdditivePipe[Sketch006.]]
  _Version = 2
FEATURE [PartDesign::Pad] Pad
  BaseFeature = -> MultiTransform001
  Direction = (0,0,1)
  Length = 22
  Length2 = 10
  Placement = pos=(0,0,0) rot=(0.57735,0.57735,0.57735;2.0944rad)
  Profile = -> Binder
  Type = 0
  expr: Length = dd.ddStorage_height - 6mm
FEATURE [PartDesign::Body] Body001  label="Blank Storage"
  Group = -> [Sketch005,Sketch006,AdditivePipe,DatumPlane,Sketch007,Pocket,Sketch008,Pad001,Sketch009,Sketch010,Sketch011,Sketch012,SubtractiveLoft001,Sketch013,Hole,Sketch014,MultiTransform001,LinearPattern002,LinearPattern003,Pad,Binder]
  Origin = -> Origin001
  Tip = -> Pad
FEATURE [PartDesign::Plane] DatumPlane001
  AttachmentOffset = pos=(0,-20,19) rot=(1,0,0;-0.523599rad)
  Length = 307.603
  MapMode = 2
  Placement = pos=(0,-20,19) rot=(1,0,0;5.75959rad)
  ResizeMode = 0
  Support = -> [XY_Plane002]
  Width = 115.126
FEATURE [Sketcher::SketchObject] Sketch016  label="Caliper master sketch"
  AttachmentOffset = pos=(0,0,4) rot=(0,0,1;0rad)
  FullyConstrained = true
  MapMode = 5
  Placement = pos=(0,-18,22.4641) rot=(-1,0,0;0.523599rad)
  Support = -> [DatumPlane001]
  sketch-geometry (16):
    g0: LineSegment StartX=7 StartY=37.5 StartZ=0 EndX=152 EndY=37.5 EndZ=0
    g1: LineSegment StartX=152 StartY=33 StartZ=0 EndX=7 EndY=33 EndZ=0
    g2: LineSegment StartX=7 StartY=33 StartZ=0 EndX=7 EndY=37.5 EndZ=0
    g3: LineSegment StartX=154 StartY=40.5 StartZ=0 EndX=242 EndY=40.5 EndZ=0
    g4: LineSegment StartX=227 StartY=20.5 StartZ=0 EndX=154 EndY=20.5 EndZ=0
    g5: LineSegment StartX=231 StartY=32.5 StartZ=0 EndX=242 EndY=32.5 EndZ=0
    g6: LineSegment StartX=244 StartY=34.5 StartZ=0 EndX=244 EndY=38.5 EndZ=0
    g7: ArcOfCircle CenterX=154 CenterY=38.5 CenterZ=0 NormalX=0 NormalY=0 NormalZ=1 AngleXU=0 Radius=2 StartAngle=1.5708 EndAngle=3.14159
    g8: ArcOfCircle CenterX=227 CenterY=22.5 CenterZ=0 NormalX=0 NormalY=0 NormalZ=1 AngleXU=0 Radius=2 StartAngle=4.71239 EndAngle=6.28319
    g9: ArcOfCircle CenterX=242 CenterY=34.5 CenterZ=0 NormalX=0 NormalY=0 NormalZ=1 AngleXU=0 Radius=2 StartAngle=4.71239 EndAngle=6.28319
    g10: ArcOfCircle CenterX=242 CenterY=38.5 CenterZ=0 NormalX=0 NormalY=0 NormalZ=1 AngleXU=0 Radius=2 StartAngle=-5.06e-14 EndAngle=1.5708
    g11: LineSegment StartX=152 StartY=37.5 StartZ=0 EndX=152 EndY=38.5 EndZ=0
    g12: LineSegment StartX=152 StartY=33 StartZ=0 EndX=152 EndY=22.5 EndZ=0
    g13: LineSegment StartX=229 StartY=30.5 StartZ=0 EndX=229 EndY=22.5 EndZ=0
    g14: ArcOfCircle CenterX=231 CenterY=30.5 CenterZ=0 NormalX=0 NormalY=0 NormalZ=1 AngleXU=0 Radius=2 StartAngle=1.5708 EndAngle=3.14159
    g15: ArcOfCircle CenterX=154 CenterY=22.5 CenterZ=0 NormalX=0 NormalY=0 NormalZ=1 AngleXU=0 Radius=2 StartAngle=3.14159 EndAngle=4.71239
  constraints (42):
    c: Coincident(g1,g2)
    c: Coincident(g2,g0)
    c: Horizontal(g0)
    c: Horizontal(g1)
    c: Vertical(g2)
    c: Horizontal(g3)
    c: Horizontal(g4)
    c: Horizontal(g5)
    c: Vertical(g6)
    c: Tangent(g3,g7) = 1.5708
    c: Tangent(g4,g8) = 1.5708
    c: Tangent(g5,g9) = -1.5708
    c: Tangent(g6,g9) = -1.5708
    c: Tangent(g6,g10) = -1.5708
    c: Coincident(g11,g0)
    c: Vertical(g11)
    c: Coincident(g12,g1)
    c: Vertical(g12)
    c: Vertical(g1,g0)
    c: Equal(g10,g9)
    c: Vertical(g13)
    c: Tangent(g5,g14) = 1.5708
    c: Tangent(g13,g14) = -1.5708
    c: Tangent(g4,g15) = 1.5708
    c: Tangent(g12,g15) = -1.5708
    c: DistanceY(g4,g3) = 20
    c: Equal(g15,g7)
    c: Equal(g7,g8)
    c: Tangent(g11,g7) = 1.5708
    c: Radius(g7) = 2
    c: DistanceY(g5,g3) = 8
    c: DistanceX(g12,g8) = 77
    c: Radius(g10) = 2
    c: DistanceX(g-1,g1) = 7
    c: DistanceY(g2,g2) = 4.5
    c: DistanceY(g0,g3) = 3
    c: DistanceY(g-1,g1) = 33
    c: DistanceX(g1,g1) = 145
    c: DistanceX(g13,g6) = 15
    c: Tangent(g3,g10) = 1.5708
    c: Tangent(g13,g8) = 1.5708
    c: Equal(g8,g14)
FEATURE [Sketcher::SketchObject] Sketch017  label="Caliper stem sketch"
  AttachmentOffset = pos=(0,0,24) rot=(0,0,1;0rad)
  ExternalGeometry = -> [Sketch016]
  FullyConstrained = true
  MapMode = 5
  Placement = pos=(0,-8,39.7846) rot=(-1,0,0;0.523599rad)
  Support = -> [DatumPlane001]
  sketch-geometry (4):
    g0: LineSegment StartX=7 StartY=37.5 StartZ=0 EndX=152 EndY=37.5 EndZ=0
    g1: LineSegment StartX=152 StartY=37.5 StartZ=0 EndX=152 EndY=33 EndZ=0
    g2: LineSegment StartX=152 StartY=33 StartZ=0 EndX=7 EndY=33 EndZ=0
    g3: LineSegment StartX=7 StartY=33 StartZ=0 EndX=7 EndY=37.5 EndZ=0
  constraints (10):
    c: Coincident(g0,g1)
    c: Coincident(g1,g2)
    c: Coincident(g2,g3)
    c: Coincident(g3,g0)
    c: Horizontal(g0)
    c: Horizontal(g2)
    c: Vertical(g1)
    c: Vertical(g3)
    c: Coincident(g0,g-3)
    c: Coincident(g1,g-4)
FEATURE [Sketcher::SketchObject] Sketch018  label="Caliper body sketch"
  AttachmentOffset = pos=(0,0,8) rot=(0,0,1;0rad)
  ExternalGeometry = -> [Sketch016]
  FullyConstrained = true
  MapMode = 5
  Placement = pos=(0,-16,25.9282) rot=(-1,0,0;0.523599rad)
  Support = -> [DatumPlane001]
  sketch-geometry (12):
    g0: LineSegment StartX=154 StartY=20.5 StartZ=0 EndX=227 EndY=20.5 EndZ=0
    g1: LineSegment StartX=229 StartY=22.5 StartZ=0 EndX=229 EndY=30.5 EndZ=0
    g2: LineSegment StartX=231 StartY=32.5 StartZ=0 EndX=242 EndY=32.5 EndZ=0
    g3: LineSegment StartX=244 StartY=34.5 StartZ=0 EndX=244 EndY=38.5 EndZ=0
    g4: LineSegment StartX=242 StartY=40.5 StartZ=0 EndX=154 EndY=40.5 EndZ=0
    g5: ArcOfCircle CenterX=154 CenterY=38.5 CenterZ=0 NormalX=0 NormalY=0 NormalZ=1 AngleXU=0 Radius=2 StartAngle=1.5708 EndAngle=3.14159
    g6: ArcOfCircle CenterX=154 CenterY=22.5 CenterZ=0 NormalX=0 NormalY=0 NormalZ=1 AngleXU=0 Radius=2 StartAngle=3.1416 EndAngle=4.71239
    g7: ArcOfCircle CenterX=227 CenterY=22.5 CenterZ=0 NormalX=0 NormalY=0 NormalZ=1 AngleXU=0 Radius=2 StartAngle=4.71239 EndAngle=6.28319
    g8: ArcOfCircle CenterX=231 CenterY=30.5 CenterZ=0 NormalX=0 NormalY=0 NormalZ=1 AngleXU=0 Radius=2 StartAngle=1.5708 EndAngle=3.14159
    g9: ArcOfCircle CenterX=242 CenterY=34.5 CenterZ=0 NormalX=0 NormalY=0 NormalZ=1 AngleXU=0 Radius=2 StartAngle=4.71239 EndAngle=6.28319
    g10: ArcOfCircle CenterX=242 CenterY=38.5 CenterZ=0 NormalX=0 NormalY=0 NormalZ=1 AngleXU=0 Radius=2 StartAngle=-4.88e-14 EndAngle=1.5708
    g11: LineSegment StartX=152 StartY=22.5 StartZ=0 EndX=152 EndY=38.5 EndZ=0
  constraints (30):
    c: Coincident(g0,g-6)
    c: Coincident(g0,g-9)
    c: Coincident(g1,g-9)
    c: Coincident(g1,g-10)
    c: Coincident(g2,g-11)
    c: Coincident(g2,g-12)
    c: Coincident(g3,g-13)
    c: Coincident(g3,g-14)
    c: Coincident(g4,g-14)
    c: Coincident(g4,g-7)
    c: Coincident(g5,g-3)
    c: Coincident(g5,g4)
    c: Coincident(g5,g-3)
    c: Coincident(g6,g-5)
    c: Coincident(g6,g0)
    c: Coincident(g7,g-9)
    c: Coincident(g7,g0)
    c: Coincident(g7,g1)
    c: Coincident(g8,g-10)
    c: Coincident(g8,g1)
    c: Coincident(g8,g2)
    c: Coincident(g9,g-12)
    c: Coincident(g9,g2)
    c: Coincident(g9,g3)
    c: Coincident(g10,g-14)
    c: Coincident(g10,g3)
    c: Coincident(g10,g4)
    c: Coincident(g11,g6)
    c: Coincident(g11,g5)
    c: Vertical(g11)
FEATURE [Sketcher::SketchObject] Sketch020  label="Caliper tip sketch"
  AttachmentOffset = pos=(0,0,3) rot=(0,0,1;0rad)
  ExternalGeometry = -> [Sketch016]
  FullyConstrained = true
  MapMode = 5
  Placement = pos=(0,-18.5,21.5981) rot=(-1,0,0;0.523599rad)
  Support = -> [DatumPlane001]
  sketch-geometry (6):
    g0: LineSegment StartX=244 StartY=34.5 StartZ=0 EndX=244 EndY=38.5 EndZ=0
    g1: LineSegment StartX=242 StartY=32.5 StartZ=0 EndX=231 EndY=32.5 EndZ=0
    g2: LineSegment StartX=231 StartY=32.5 StartZ=0 EndX=231 EndY=40.5 EndZ=0
    g3: LineSegment StartX=231 StartY=40.5 StartZ=0 EndX=242 EndY=40.5 EndZ=0
    g4: ArcOfCircle CenterX=242 CenterY=38.5 CenterZ=0 NormalX=0 NormalY=0 NormalZ=1 AngleXU=0 Radius=2 StartAngle=-4.8e-14 EndAngle=1.5708
    g5: ArcOfCircle CenterX=242 CenterY=34.5 CenterZ=0 NormalX=0 NormalY=0 NormalZ=1 AngleXU=0 Radius=2 StartAngle=4.71239 EndAngle=6.28319
  constraints (15):
    c: Coincident(g0,g-3)
    c: Coincident(g0,g-4)
    c: Coincident(g1,g-5)
    c: Coincident(g1,g-5)
    c: Coincident(g2,g1)
    c: Vertical(g2)
    c: Coincident(g3,g2)
    c: Coincident(g3,g-4)
    c: Coincident(g4,g-4)
    c: Coincident(g4,g3)
    c: Coincident(g4,g0)
    c: Coincident(g5,g-3)
    c: Coincident(g5,g0)
    c: Coincident(g5,g1)
    c: Horizontal(g3)
FEATURE [PartDesign::FeatureBase] BaseFeature  label="Unnamed"
  BaseFeature = -> BaseFeature
FEATURE [PartDesign::FeatureBase] Clone001
  BaseFeature = -> BaseFeature
  Placement = pos=(0,0,0) rot=(0.57735,0.57735,0.57735;2.0944rad)
FEATURE [PartDesign::Pocket] Pocket006
  BaseFeature = -> Clone001
  Direction = (0,-0.5,-0.866025)
  Length = 5
  Length2 = 5
  Placement = pos=(0,0,0) rot=(0.57735,0.57735,0.57735;2.0944rad)
  Profile = -> Sketch020
  ReferenceAxis = -> Sketch020 [N_Axis]
  Reversed = true
  Type = 1
FEATURE [PartDesign::Pocket] Pocket003
  BaseFeature = -> Pocket006
  Direction = (0,-0.5,-0.866025)
  Length = 5
  Length2 = 5
  Placement = pos=(0,0,0) rot=(0.57735,0.57735,0.57735;2.0944rad)
  Profile = -> Sketch017
  ReferenceAxis = -> Sketch017 [N_Axis]
  Reversed = true
  Type = 1
FEATURE [PartDesign::Pocket] Pocket004
  BaseFeature = -> Pocket003
  Direction = (0,-0.5,-0.866025)
  Length = 5
  Length2 = 5
  Placement = pos=(0,0,0) rot=(0.57735,0.57735,0.57735;2.0944rad)
  Profile = -> Sketch018
  ReferenceAxis = -> Sketch018 [N_Axis]
  Reversed = true
  Type = 1
FEATURE [PartDesign::Pocket] Pocket005
  BaseFeature = -> Pocket004
  Direction = (0,1,2e-16)
  Length = 3.5
  Length2 = 5
  Placement = pos=(0,0,0) rot=(0.57735,0.57735,0.57735;2.0944rad)
  Profile = -> Sketch019
  ReferenceAxis = -> Sketch019 [N_Axis]
  Reversed = true
  Type = 0
FEATURE [PartDesign::LinearPattern] LinearPattern
  BaseFeature = -> Pocket005
  Direction = -> Sketch019 [H_Axis]
  Length = 120
  Occurrences = 6
  Originals = -> [Pocket005]
  Placement = pos=(0,0,0) rot=(0.57735,0.57735,0.57735;2.0944rad)
  Refine = true
FEATURE [PartDesign::Fillet] Fillet
  Base = -> LinearPattern [Face271,Face273]
  BaseFeature = -> LinearPattern
  Placement = pos=(0,0,0) rot=(0.57735,0.57735,0.57735;2.0944rad)
  Radius = 2
  SupportTransform = false
  UseAllEdges = false
FEATURE [PartDesign::Fillet] Fillet001
  Base = -> Fillet [Face4]
  BaseFeature = -> Fillet
  Placement = pos=(0,0,0) rot=(0.57735,0.57735,0.57735;2.0944rad)
  Radius = 0.4
  SupportTransform = false
  UseAllEdges = false
FEATURE [PartDesign::Body] Body002  label="Caliper holder"
  BaseFeature = -> BaseFeature
  Group = -> [BaseFeature,DatumPlane001,Clone001,Sketch016,Pocket006,Sketch017,Sketch018,Pocket003,Pocket004,Sketch019,Pocket005,LinearPattern,Sketch020,Fillet,Fillet001]
  Origin = -> Origin002
  Tip = -> Fillet001
